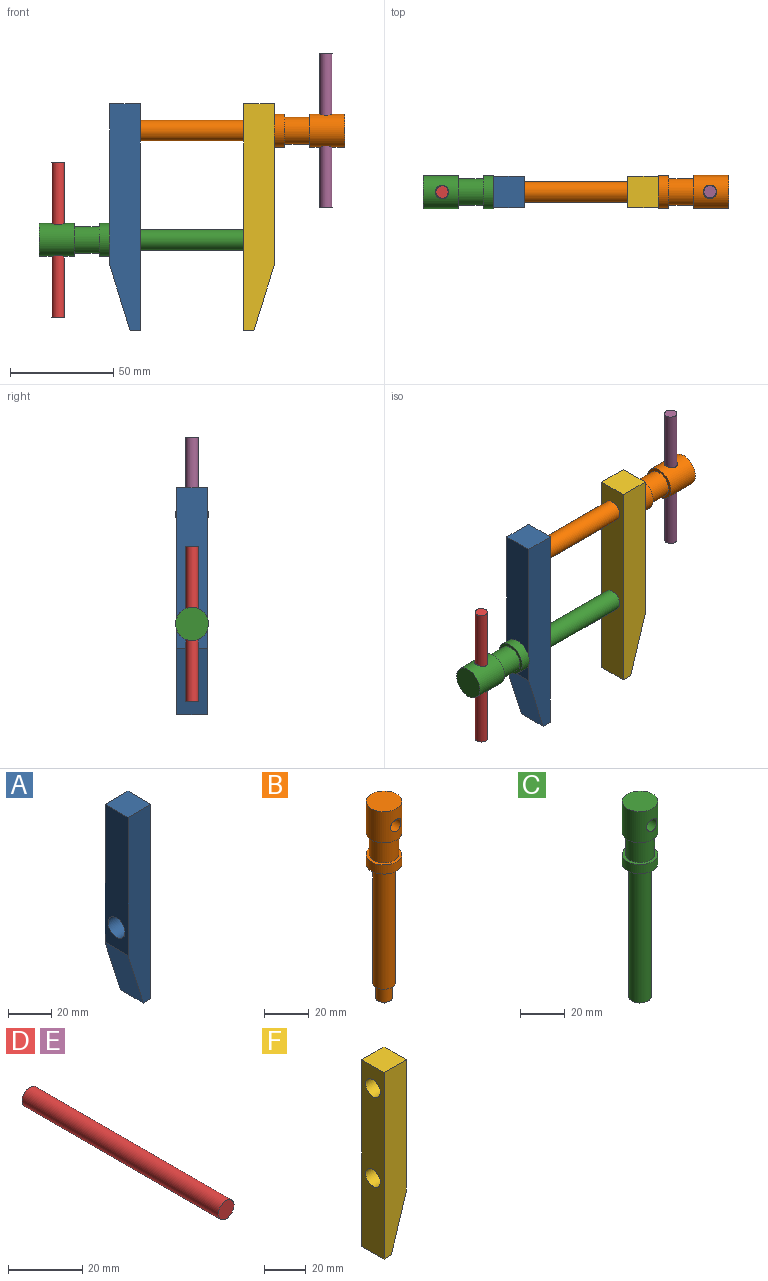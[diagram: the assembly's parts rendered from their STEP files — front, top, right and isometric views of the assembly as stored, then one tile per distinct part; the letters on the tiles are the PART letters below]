
ASSEMBLY  parts=6 mates=5
PART A: 10 faces, bbox 15x15x110 mm
  f0: plane 15x15mm, normal (0,0,1), area 225mm2, adj f1,f4,f5,f6
  f1: plane 78x15mm, normal (-1,0,0), area 1075mm2, adj f0,f2,f5,f6,f9
  f2: plane 32x15mm, normal (-0.95,0,-0.3), area 502.9mm2, adj f1,f3,f5,f6
  f3: plane 15x5mm, normal (0,0,-1), area 75mm2, adj f2,f4,f5,f6
  f4: plane 110x15mm, normal (1,0,0), area 1504.7mm2, adj f0,f3,f5,f6,f7,f9
  f5: plane 110x15mm, normal (0,-1,0), area 1490mm2, adj f0,f1,f2,f3,f4
  f6: plane 110x15mm, normal (0,1,0), area 1490mm2, adj f0,f1,f2,f3,f4
  f7: cylinder r=4mm len=8mm, axis (-1,0,0), area 188.5mm2, adj f4,f8
  f8: cone r=4mm half-angle=53.1deg, axis (1,0,0), area 62.8mm2, adj f7
  f9: cylinder r=5.5mm len=15mm, axis (1,0,0), area 518.4mm2, adj f1,f4
PART B: 12 faces, bbox 16x16x110 mm
  f0: cylinder r=8mm len=17mm, axis (0,0,1), area 786.8mm2, adj f1,f2,f3
  f1: plane 16x16mm, normal (0,0,-1), area 68.3mm2, adj f0,f4
  f2: plane 16x16mm, normal (0,0,1), area 201.1mm2, adj f0
  f3: cylinder r=3.25mm len=16mm, axis (0,-1,0), area 312.8mm2, adj f0
  f4: cylinder r=6.5mm len=13mm, axis (0,0,1), area 490.1mm2, adj f1,f7
  f5: cylinder r=8mm len=16mm, axis (0,0,1), area 251.3mm2, adj f6,f7
  f6: plane 16x16mm, normal (0,0,-1), area 122.5mm2, adj f5,f8
  f7: plane 16x16mm, normal (0,0,1), area 68.3mm2, adj f4,f5
  f8: cylinder r=5mm len=65mm, axis (0,0,1), area 2042mm2, adj f6,f9
  f9: plane 10x10mm, normal (0,0,-1), area 34.4mm2, adj f8,f10
  f10: cylinder r=3.75mm len=8mm, axis (0,0,1), area 188.5mm2, adj f9,f11
  f11: cone r=3.75mm half-angle=51.3deg, axis (0,0,1), area 56.6mm2, adj f10
PART C: 10 faces, bbox 16x16x107 mm
  f0: cylinder r=8mm len=17mm, axis (0,0,1), area 786.8mm2, adj f1,f2,f3
  f1: plane 16x16mm, normal (0,0,-1), area 68.3mm2, adj f0,f4
  f2: plane 16x16mm, normal (0,0,1), area 201.1mm2, adj f0
  f3: cylinder r=3.25mm len=16mm, axis (0,1,0), area 312.8mm2, adj f0
  f4: cylinder r=6.5mm len=13mm, axis (0,0,1), area 490.1mm2, adj f1,f7
  f5: cylinder r=8mm len=16mm, axis (0,0,1), area 251.3mm2, adj f6,f7
  f6: plane 16x16mm, normal (0,0,-1), area 122.5mm2, adj f5,f8
  f7: plane 16x16mm, normal (0,0,1), area 68.3mm2, adj f4,f5
  f8: cylinder r=5mm len=73mm, axis (0,0,1), area 2293.4mm2, adj f6,f9
  f9: plane 10x10mm, normal (0,0,-1), area 78.5mm2, adj f8
PART D: 3 faces, bbox 6x75x6 mm
  f0: cylinder r=3mm len=75mm, axis (0,1,0), area 1413.7mm2, adj f1,f2
  f1: plane 6x6mm, normal (0,-1,0), area 28.3mm2, adj f0
  f2: plane 6x6mm, normal (0,1,0), area 28.3mm2, adj f0
PART E: same geometry as D
PART F: 9 faces, bbox 15x15x110 mm
  f0: plane 110x15mm, normal (-1,0,0), area 1492.9mm2, adj f1,f4,f5,f6,f7,f8
  f1: plane 15x5mm, normal (0,0,-1), area 75mm2, adj f0,f2,f5,f6
  f2: plane 32x15mm, normal (0.95,0,-0.3), area 502.9mm2, adj f1,f3,f5,f6
  f3: plane 78x15mm, normal (1,0,0), area 1012.9mm2, adj f2,f4,f5,f6,f7,f8
  f4: plane 15x15mm, normal (0,0,1), area 225mm2, adj f0,f3,f5,f6
  f5: plane 110x15mm, normal (0,-1,0), area 1490mm2, adj f0,f1,f2,f3,f4
  f6: plane 110x15mm, normal (0,1,0), area 1490mm2, adj f0,f1,f2,f3,f4
  f7: cylinder r=5mm len=15mm, axis (-1,0,0), area 471.2mm2, adj f0,f3
  f8: cylinder r=5mm len=15mm, axis (-1,0,0), area 471.2mm2, adj f0,f3
PLACE A t=(-51.93,-1.38,-3.73)mm
PLACE B rot(axis=(0.58,0.58,0.58),120deg) t=(54.57,-1.38,38.27)mm
PLACE C rot(axis=(0.58,-0.58,-0.58),120deg) t=(-93.43,-1.38,-14.73)mm
PLACE D rot(axis=(0.58,-0.58,-0.58),120deg) t=(-84.43,-1.38,-14.73)mm
PLACE E rot(axis=(0.58,0.58,0.58),120deg) t=(45.57,-1.38,38.27)mm
PLACE F t=(13.07,-1.38,-3.73)mm
MATE fastened E.f0 <-> B.f3  axis (0,0,1) through (45.57,-1.38,38.27)mm
MATE revolute B.f10 <-> A.f7  axis (-1,0,0) through (-44.43,-1.38,38.27)mm
MATE revolute C.f8 <-> A.f9  axis (1,0,0) through (-59.43,-1.38,-14.73)mm
MATE fastened D.f0 <-> C.f3  axis (0,0,1) through (-84.43,-1.38,-14.73)mm
MATE revolute B.f8 <-> F.f8  axis (1,0,0) through (20.57,-1.38,38.27)mm
